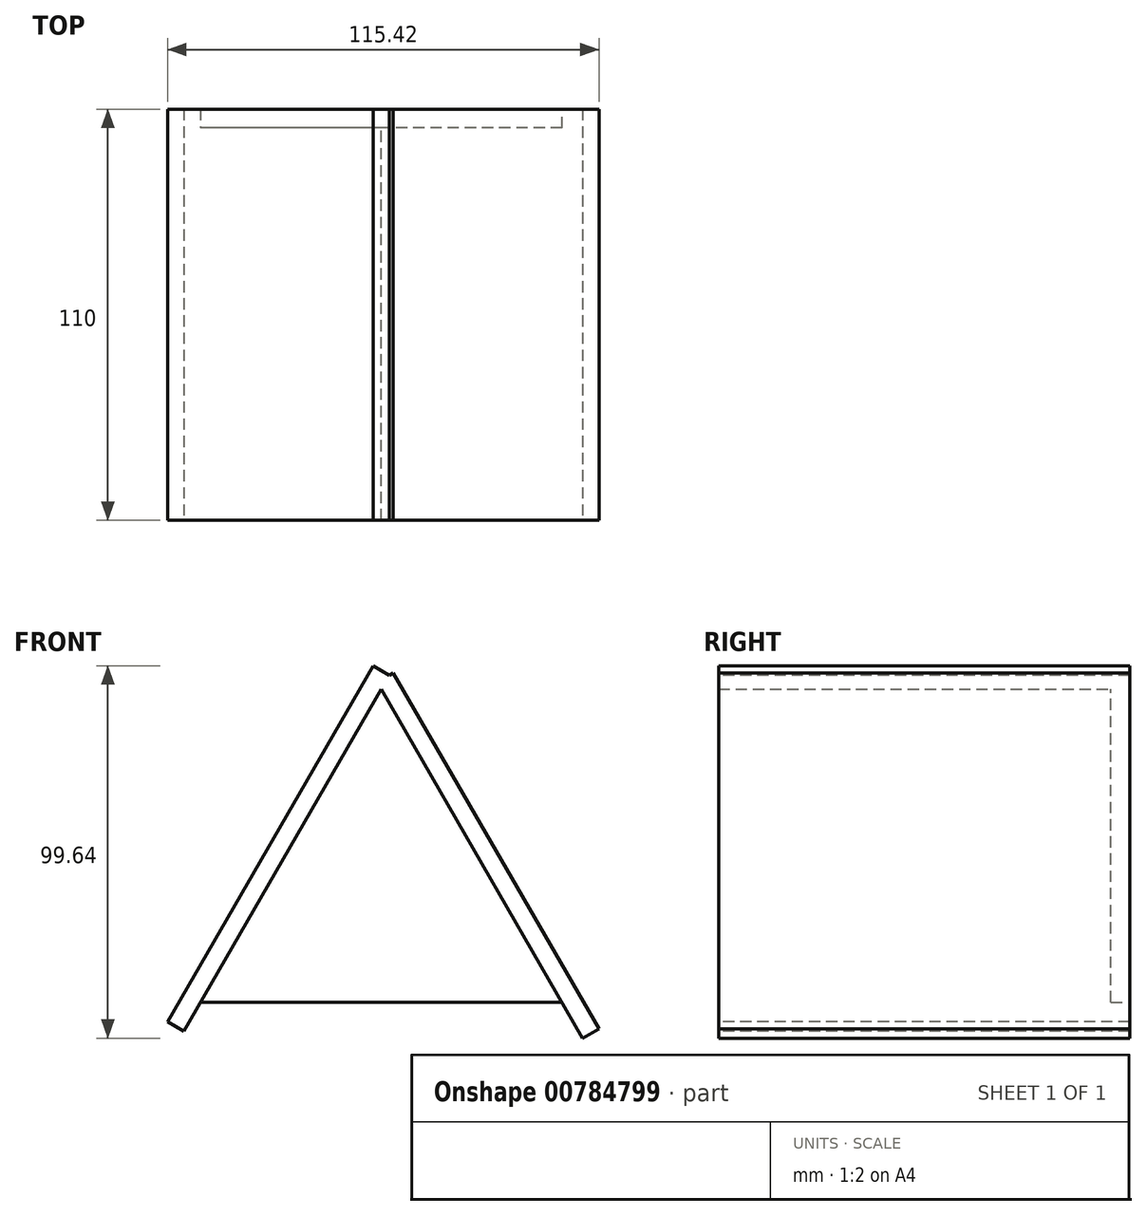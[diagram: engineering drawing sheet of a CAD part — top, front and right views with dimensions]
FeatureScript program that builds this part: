
annotation { "Feature Type Name" : "Feature", "Feature Type Description" : "" }
export const myFeature = defineFeature(function(context is Context, id is Id, definition is map)
    precondition{}
    {
        {
            var Q0;
            Q0=qCreatedBy(makeId("Front.planeOp"),FACE);
            var sketch = newSketch(context, id + "F0", { "sketchPlane" : qUnion([Q0])});
            skCircle(sketch, "E0.cCircle", {"center": v(0, 0) * mm, "radius": 59.18 * mm, "construction": true});
            skLineSegment(sketch, "E0.0", {"start": v(0, 59.18) * mm, "end": v(51.25, -29.59) * mm});
            skLineSegment(sketch, "E0.1", {"start": v(51.25, -29.59) * mm, "end": v(-51.25, -29.59) * mm});
            skLineSegment(sketch, "E0.2", {"start": v(-51.25, -29.59) * mm, "end": v(0, 59.18) * mm});
            skSolve(sketch);
        }
        {
            var Q0;
            Q0=makeQuery(id+"F0.imprint","IMPRINT",FACE,{"disambiguationData":[TD([[makeQuery(id+"F0.imprint","IMPRINT",EDGE,{"derivedFrom":sQuery(id+"F0.wireOp",EDGE,"E0.0")}),-1.0]])]});
            extrude(context, id + "F1", {"entities" : qUnion([Q0]), "oppositeDirection" : true, "depth" : 5 * mm, "offsetDistance" : 25 * mm});
        }
        {
            var Q0;
            Q0=makeQuery(id+"F1.opExtrude","SWEPT_FACE",FACE,{"disambiguationData":[OSD([sQuery(id+"F0.wireOp",EDGE,"E0.2")])]});
            var sketch = newSketch(context, id + "F2", { "sketchPlane" : qUnion([Q0])});
            skLineSegment(sketch, "E1.bottom", {"start": v(-5, 51.25) * mm, "end": v(105, 51.25) * mm});
            skLineSegment(sketch, "E1.top", {"start": v(-5, -58.75) * mm, "end": v(105, -58.75) * mm});
            skLineSegment(sketch, "E1.left", {"start": v(-5, 51.25) * mm, "end": v(-5, -58.75) * mm});
            skLineSegment(sketch, "E1.right", {"start": v(105, 51.25) * mm, "end": v(105, -58.75) * mm});
            skSolve(sketch);
        }
        {
            var Q0;
            Q0 = qSketchRegion(id + "F2", true);
            extrude(context, id + "F3", {"entities" : qUnion([Q0]), "operationType" : NewBodyOperationType.ADD, "endBound" : BoundingType.SYMMETRIC, "depth" : 5 * mm, "offsetDistance" : 25 * mm});
        }
        {
            var Q0;
            Q0=makeQuery(id+"F1.opExtrude","SWEPT_FACE",FACE,{"disambiguationData":[OSD([sQuery(id+"F0.wireOp",EDGE,"E0.0")])]});
            var sketch = newSketch(context, id + "F4", { "sketchPlane" : qUnion([Q0])});
            skLineSegment(sketch, "E2.bottom", {"start": v(5, 49.08) * mm, "end": v(-105, 49.08) * mm});
            skLineSegment(sketch, "E2.top", {"start": v(5, -60.92) * mm, "end": v(-105, -60.92) * mm});
            skLineSegment(sketch, "E2.left", {"start": v(5, 49.08) * mm, "end": v(5, -60.92) * mm});
            skLineSegment(sketch, "E2.right", {"start": v(-105, 49.08) * mm, "end": v(-105, -60.92) * mm});
            skSolve(sketch);
        }
        {
            var Q0;
            Q0 = qSketchRegion(id + "F4", true);
            extrude(context, id + "F5", {"entities" : qUnion([Q0]), "operationType" : NewBodyOperationType.ADD, "endBound" : BoundingType.SYMMETRIC, "depth" : 5 * mm, "offsetDistance" : 25 * mm});
        }
    });
